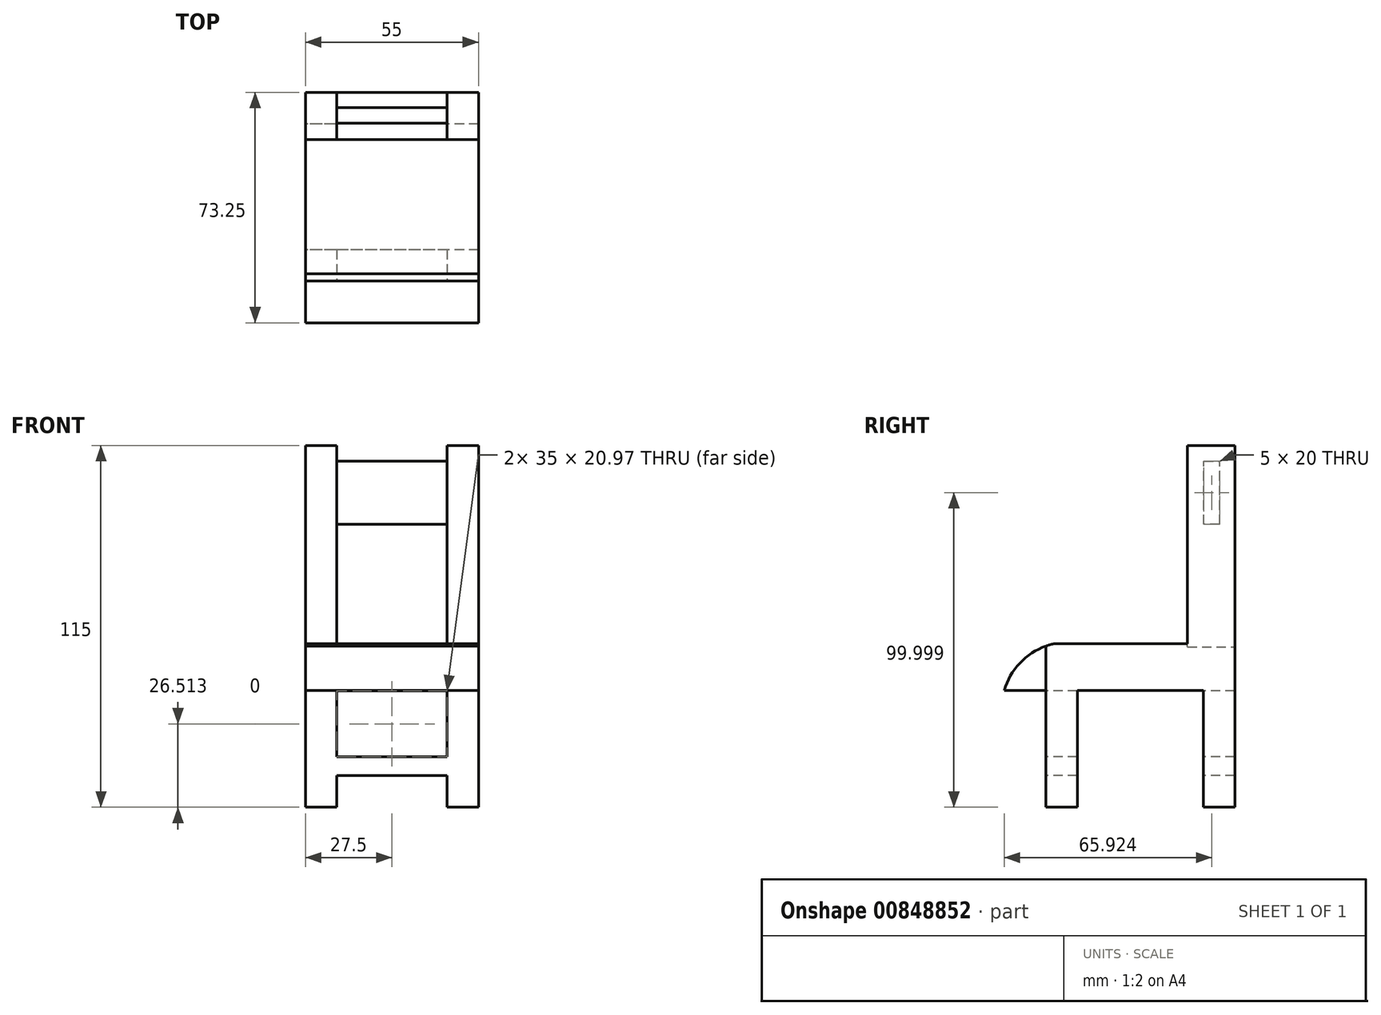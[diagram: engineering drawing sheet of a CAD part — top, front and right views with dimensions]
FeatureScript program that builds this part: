
annotation { "Feature Type Name" : "Feature", "Feature Type Description" : "" }
export const myFeature = defineFeature(function(context is Context, id is Id, definition is map)
    precondition{}
    {
        {
            var Q0;
            Q0=qCreatedBy(makeId("Right.planeOp"),FACE);
            var sketch = newSketch(context, id + "F0", { "sketchPlane" : qUnion([Q0])});
            skLineSegment(sketch, "E0", {"start": v(0, 52.93) * mm, "end": v(0, -62.07) * mm});
            skLineSegment(sketch, "E1", {"start": v(0, -62.07) * mm, "end": v(-60, -62.07) * mm});
            skLineSegment(sketch, "E2", {"start": v(-60, -62.07) * mm, "end": v(-60, 52.93) * mm});
            skLineSegment(sketch, "E3", {"start": v(-60, 52.93) * mm, "end": v(0, 52.93) * mm});
            skSolve(sketch);
        }
        {
            var Q0;
            Q0=makeQuery(id+"F0.imprint","IMPRINT",FACE,{"disambiguationData":[TD([[makeQuery(id+"F0.imprint","IMPRINT",EDGE,{"derivedFrom":sQuery(id+"F0.wireOp",EDGE,"E0")}),-1.0]])]});
            extrude(context, id + "F1", {"entities" : qUnion([Q0]), "depth" : 55 * mm, "offsetDistance" : 25 * mm});
        }
        {
            var Q0;
            Q0=makeQuery(id+"F1.opExtrude","SWEPT_FACE",FACE,{"disambiguationData":[OSD([sQuery(id+"F0.wireOp",EDGE,"E2")])]});
            var sketch = newSketch(context, id + "F2", { "sketchPlane" : qUnion([Q0])});
            skLineSegment(sketch, "E4", {"start": v(0, -62.07) * mm, "end": v(10, -62.07) * mm});
            skLineSegment(sketch, "E5", {"start": v(45, -62.07) * mm, "end": v(55, -62.07) * mm});
            skLineSegment(sketch, "E6", {"start": v(10, -62.07) * mm, "end": v(10, -52.03) * mm});
            skLineSegment(sketch, "E7", {"start": v(10, -52.03) * mm, "end": v(45, -52.03) * mm});
            skLineSegment(sketch, "E8", {"start": v(45, -52.03) * mm, "end": v(45, -46.04) * mm});
            skLineSegment(sketch, "E9", {"start": v(45, -46.04) * mm, "end": v(10, -46.04) * mm});
            skLineSegment(sketch, "E10", {"start": v(10, -46.04) * mm, "end": v(10, -52.03) * mm});
            skLineSegment(sketch, "E11", {"start": v(45, -52.03) * mm, "end": v(45, -62.07) * mm});
            skLineSegment(sketch, "E12", {"start": v(0, -62.07) * mm, "end": v(0, -25.07) * mm});
            skLineSegment(sketch, "E13", {"start": v(0, -25.07) * mm, "end": v(55, -25.07) * mm});
            skLineSegment(sketch, "E14", {"start": v(55, -25.07) * mm, "end": v(55, -62.07) * mm});
            skLineSegment(sketch, "E15", {"start": v(0, -25.07) * mm, "end": v(0, -62.07) * mm});
            skLineSegment(sketch, "E16", {"start": v(10, -46.04) * mm, "end": v(10, -25.07) * mm});
            skLineSegment(sketch, "E17", {"start": v(45, -46.04) * mm, "end": v(45, -25.07) * mm});
            skSolve(sketch);
        }
        {
            var Q0;
            {var subQ0=sQuery(id+"F2.wireOp",EDGE,"E6");Q0=makeQuery(id+"F2.imprint","IMPRINT",FACE,{"disambiguationData":[TD([[makeQuery(id+"F2.imprint","IMPRINT",EDGE,{"derivedFrom":subQ0}),-1.0]])]});}
            extrude(context, id + "F3", {"entities" : qUnion([Q0]), "operationType" : NewBodyOperationType.REMOVE, "oppositeDirection" : true, "depth" : 90 * mm, "offsetDistance" : 25 * mm});
        }
        {
            var Q0;
            Q0=makeQuery(id+"F2.imprint","IMPRINT",FACE,{"disambiguationData":[TD([[makeQuery(id+"F2.imprint","IMPRINT",EDGE,{"derivedFrom":sQuery(id+"F2.wireOp",EDGE,"E9")}),-1.0]])]});
            extrude(context, id + "F4", {"entities" : qUnion([Q0]), "operationType" : NewBodyOperationType.REMOVE, "oppositeDirection" : true, "depth" : 96 * mm, "offsetDistance" : 25 * mm});
        }
        {
            var Q0;
            Q0=makeQuery(id+"F1.opExtrude","SWEPT_FACE",FACE,{"disambiguationData":[OSD([sQuery(id+"F0.wireOp",EDGE,"E0")])]});
            var sketch = newSketch(context, id + "F5", { "sketchPlane" : qUnion([Q0])});
            skLineSegment(sketch, "E18", {"start": v(0, -25.07) * mm, "end": v(0, -10.07) * mm});
            skSolve(sketch);
        }
        {
            var Q0;
            Q0=makeQuery(id+"F1.opExtrude","CAP_FACE",FACE,{"disambiguationData":[OSD([sQuery(id+"F0.wireOp",EDGE,"E0"),sQuery(id+"F0.wireOp",EDGE,"E1"),sQuery(id+"F0.wireOp",EDGE,"E2"),sQuery(id+"F0.wireOp",EDGE,"E3")])],"isStart":true});
            var sketch = newSketch(context, id + "F6", { "sketchPlane" : qUnion([Q0])});
            skLineSegment(sketch, "E19", {"start": v(0, -10.11) * mm, "end": v(57.6, -10.11) * mm});
            skLineSegment(sketch, "E20", {"start": v(0, -24.87) * mm, "end": v(60, -24.87) * mm});
            skLineSegment(sketch, "E21", {"start": v(60, -24.87) * mm, "end": v(73.25, -24.87) * mm});
            skArc(sketch, "E22", {"start": v(73.25, -24.87) * mm, "mid": v(67.43, -15.37) * mm, "end": v(57.6, -10.11) * mm});
            skLineSegment(sketch, "E23", {"start": v(0, -10.11) * mm, "end": v(0, -24.87) * mm});
            skSolve(sketch);
        }
        {
            var Q0;
            {var subQ0=sQuery(id+"F6.wireOp",EDGE,"E21");Q0=makeQuery(id+"F6.imprint","IMPRINT",FACE,{"disambiguationData":[TD([[makeQuery(id+"F6.imprint","IMPRINT",EDGE,{"derivedFrom":subQ0}),1.0]])]});}
            extrude(context, id + "F7", {"entities" : qUnion([Q0]), "oppositeDirection" : true, "depth" : 55 * mm, "offsetDistance" : 25 * mm});
        }
        {
            var Q0;
            {var subQ2=sQuery(id+"F6.wireOp",EDGE,"E19");Q0=makeQuery(id+"F6.imprint","IMPRINT",FACE,{"disambiguationData":[TD([[makeQuery(id+"F6.imprint","IMPRINT",EDGE,{"derivedFrom":subQ2}),1.0]])]});}
            var sketch = newSketch(context, id + "F8", { "sketchPlane" : qUnion([Q0])});
            skLineSegment(sketch, "E24", {"start": v(0, -10.11) * mm, "end": v(15, -10.11) * mm});
            skLineSegment(sketch, "E25", {"start": v(15, -10.11) * mm, "end": v(15, 52.93) * mm});
            skLineSegment(sketch, "E26", {"start": v(15, 52.93) * mm, "end": v(0, 52.93) * mm});
            skLineSegment(sketch, "E27", {"start": v(0, 52.93) * mm, "end": v(0, -10.11) * mm});
            skSolve(sketch);
        }
        {
            var Q0;
            {var subQ6=sQuery(id+"F8.wireOp",EDGE,"E25");Q0=makeQuery(id+"F8.imprint","IMPRINT",FACE,{"disambiguationData":[TD([[makeQuery(id+"F8.imprint","IMPRINT",EDGE,{"derivedFrom":subQ6}),-1.0]])]});}
            extrude(context, id + "F9", {"entities" : qUnion([Q0]), "operationType" : NewBodyOperationType.REMOVE, "oppositeDirection" : true, "depth" : 95 * mm, "offsetDistance" : 25 * mm});
        }
        {
            var Q0;
            Q0=makeQuery(id+"F1.opExtrude","SWEPT_FACE",FACE,{"disambiguationData":[OSD([sQuery(id+"F0.wireOp",EDGE,"E3")])]});
            var sketch = newSketch(context, id + "F10", { "sketchPlane" : qUnion([Q0])});
            skLineSegment(sketch, "E28", {"start": v(55, -15) * mm, "end": v(45, -15) * mm});
            skLineSegment(sketch, "E29", {"start": v(45, -15) * mm, "end": v(45, 0) * mm});
            skLineSegment(sketch, "E30", {"start": v(45, 0) * mm, "end": v(55, 0) * mm});
            skLineSegment(sketch, "E31", {"start": v(55, 0) * mm, "end": v(55, -15) * mm});
            skLineSegment(sketch, "E32", {"start": v(0, -15) * mm, "end": v(10, -15) * mm});
            skLineSegment(sketch, "E33", {"start": v(10, -15) * mm, "end": v(10, 0) * mm});
            skLineSegment(sketch, "E34", {"start": v(10, 0) * mm, "end": v(0, 0) * mm});
            skLineSegment(sketch, "E35", {"start": v(0, 0) * mm, "end": v(0, -15) * mm});
            skSolve(sketch);
        }
        {
            var Q0;
            {var subQ0=sQuery(id+"F10.wireOp",EDGE,"E29");Q0=makeQuery(id+"F10.imprint","IMPRINT",FACE,{"disambiguationData":[TD([[makeQuery(id+"F10.imprint","IMPRINT",EDGE,{"derivedFrom":subQ0}),1.0]])]});}
            extrude(context, id + "F11", {"entities" : qUnion([Q0]), "operationType" : NewBodyOperationType.REMOVE, "oppositeDirection" : true, "depth" : 5 * mm, "offsetDistance" : 25 * mm});
        }
        {
            var Q0;
            Q0=makeQuery(id+"F11.boolean.opBoolean","COPY",FACE,{"derivedFrom":makeQuery(id+"F11.opExtrude","CAP_FACE",FACE,{"disambiguationData":[OSD([sQuery(id+"F0.wireOp",EDGE,"E0"),sQuery(id+"F0.wireOp",EDGE,"E3"),sQuery(id+"F8.wireOp",EDGE,"E25"),sQuery(id+"F8.wireOp",EDGE,"E26"),sQuery(id+"F10.wireOp",EDGE,"E29"),sQuery(id+"F10.wireOp",EDGE,"E33")])],"isStart":false})});
            var sketch = newSketch(context, id + "F12", { "sketchPlane" : qUnion([Q0])});
            skLineSegment(sketch, "E36", {"start": v(10, 0) * mm, "end": v(10, -4.83) * mm});
            skLineSegment(sketch, "E37", {"start": v(10, -9.83) * mm, "end": v(10, -15) * mm});
            skLineSegment(sketch, "E38", {"start": v(10, -4.83) * mm, "end": v(45, -4.83) * mm});
            skLineSegment(sketch, "E39", {"start": v(45, -4.83) * mm, "end": v(45, -9.83) * mm});
            skLineSegment(sketch, "E40", {"start": v(45, -9.83) * mm, "end": v(10, -9.83) * mm});
            skLineSegment(sketch, "E41", {"start": v(10, -4.83) * mm, "end": v(10, -9.83) * mm});
            skSolve(sketch);
        }
        {
            var Q0;
            Q0=makeQuery(id+"F12.imprint","IMPRINT",FACE,{"disambiguationData":[TD([[makeQuery(id+"F12.imprint","IMPRINT",EDGE,{"derivedFrom":sQuery(id+"F12.wireOp",EDGE,"E36")}),-1.0]])]});
            var Q1;
            Q1=makeQuery(id+"F12.imprint","IMPRINT",FACE,{"disambiguationData":[TD([[makeQuery(id+"F12.imprint","IMPRINT",EDGE,{"derivedFrom":sQuery(id+"F12.wireOp",EDGE,"E37")}),-1.0]])]});
            extrude(context, id + "F13", {"entities" : qUnion([Q0, Q1]), "operationType" : NewBodyOperationType.REMOVE, "oppositeDirection" : true, "depth" : 59 * mm, "offsetDistance" : 25 * mm});
        }
        {
            var Q0;
            Q0=makeQuery(id+"F13.boolean.opBoolean","COPY",FACE,{"derivedFrom":makeQuery(id+"F13.opExtrude","SWEPT_FACE",FACE,{"disambiguationData":[OSD([sQuery(id+"F12.wireOp",EDGE,"E40")])]})});
            var sketch = newSketch(context, id + "F14", { "sketchPlane" : qUnion([Q0])});
            skLineSegment(sketch, "E42", {"start": v(10, 47.93) * mm, "end": v(10, 27.93) * mm});
            skLineSegment(sketch, "E43", {"start": v(10, 27.93) * mm, "end": v(45, 27.93) * mm});
            skLineSegment(sketch, "E44", {"start": v(45, 27.93) * mm, "end": v(45, 47.93) * mm});
            skLineSegment(sketch, "E45", {"start": v(45, 47.93) * mm, "end": v(10, 47.93) * mm});
            skSolve(sketch);
        }
        {
            var Q0;
            {var subQ0=sQuery(id+"F14.wireOp",EDGE,"E43");Q0=makeQuery(id+"F14.imprint","IMPRINT",FACE,{"disambiguationData":[TD([[makeQuery(id+"F14.imprint","IMPRINT",EDGE,{"derivedFrom":subQ0}),-1.0]])]});}
            extrude(context, id + "F15", {"entities" : qUnion([Q0]), "operationType" : NewBodyOperationType.REMOVE, "oppositeDirection" : true, "depth" : 25 * mm, "offsetDistance" : 25 * mm});
        }
        {
            var Q0;
            {var subQ0=sQuery(id+"F6.wireOp",EDGE,"E20");Q0=makeQuery(id+"F6.imprint","IMPRINT",FACE,{"disambiguationData":[TD([[makeQuery(id+"F6.imprint","IMPRINT",EDGE,{"derivedFrom":subQ0}),-1.0]])]});}
            var sketch = newSketch(context, id + "F16", { "sketchPlane" : qUnion([Q0])});
            skLineSegment(sketch, "E46", {"start": v(60.02, -45.9) * mm, "end": v(59.83, -24.8) * mm});
            skLineSegment(sketch, "E47", {"start": v(59.83, -24.8) * mm, "end": v(0, -24.8) * mm});
            skLineSegment(sketch, "E48", {"start": v(0, -24.8) * mm, "end": v(0, -45.9) * mm});
            skLineSegment(sketch, "E49", {"start": v(0, -45.9) * mm, "end": v(10, -45.9) * mm});
            skLineSegment(sketch, "E50", {"start": v(10, -45.9) * mm, "end": v(10, -24.8) * mm});
            skLineSegment(sketch, "E51", {"start": v(60.02, -45.9) * mm, "end": v(50.02, -45.9) * mm});
            skLineSegment(sketch, "E52", {"start": v(50.02, -45.9) * mm, "end": v(50.02, -24.8) * mm});
            skLineSegment(sketch, "E53", {"start": v(50.02, -24.8) * mm, "end": v(59.83, -24.8) * mm});
            skLineSegment(sketch, "E54", {"start": v(10, -45.9) * mm, "end": v(10, -62.34) * mm});
            skLineSegment(sketch, "E55", {"start": v(10, -62.34) * mm, "end": v(50.02, -62.34) * mm});
            skLineSegment(sketch, "E56", {"start": v(50.02, -62.34) * mm, "end": v(50.02, -45.9) * mm});
            skLineSegment(sketch, "E57", {"start": v(50.02, -62.34) * mm, "end": v(60.02, -62.34) * mm});
            skLineSegment(sketch, "E58", {"start": v(60.02, -62.34) * mm, "end": v(59.83, -24.8) * mm});
            skSolve(sketch);
        }
        {
            var Q0;
            {var subQ3=makeQuery(id+"F6.imprint","IMPRINT",EDGE,{"derivedFrom":makeQuery(id+"F1.opExtrude","CAP_EDGE",EDGE,{"disambiguationData":[OSD([sQuery(id+"F0.wireOp",EDGE,"E1")])],"isStart":true})});var subQ5=sQuery(id+"F16.wireOp",EDGE,"E54");var subQ6=makeQuery(id+"F16.imprint","INTERSECT",VERTEX,{"derivedFrom":[subQ3,subQ5]});Q0=makeQuery(id+"F16.imprint","IMPRINT",FACE,{"disambiguationData":[TD([[makeQuery(id+"F16.imprint","IMPRINT",EDGE,{"disambiguationData":[TD([[subQ6,-1.0]])],"derivedFrom":subQ3}),1.0]])]});}
            extrude(context, id + "F17", {"entities" : qUnion([Q0]), "operationType" : NewBodyOperationType.REMOVE, "oppositeDirection" : true, "depth" : 95 * mm, "offsetDistance" : 25 * mm});
        }
    });
